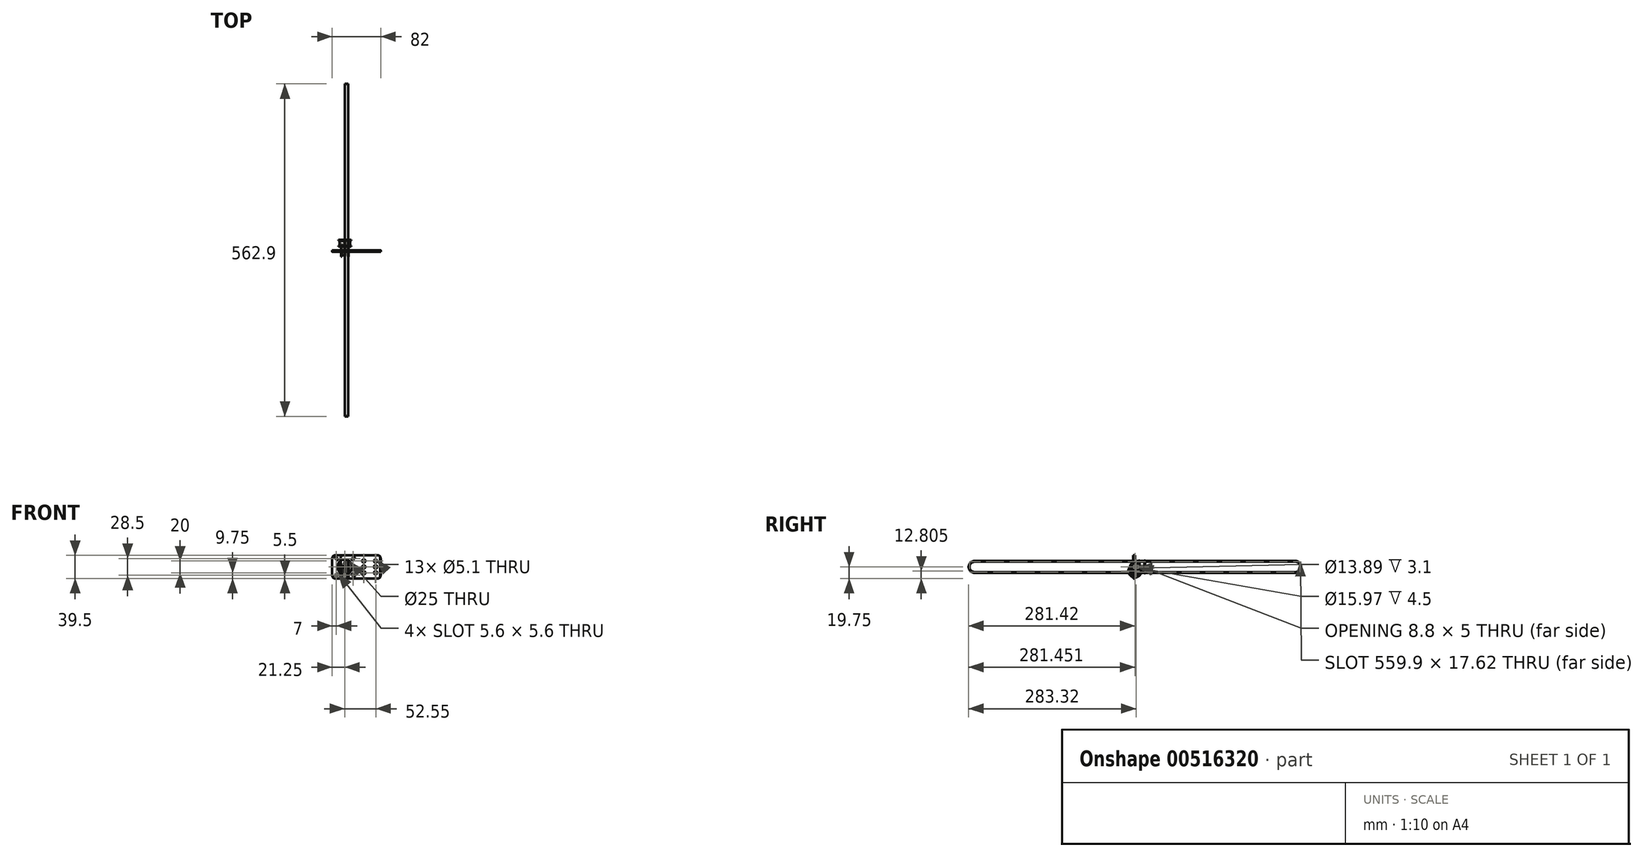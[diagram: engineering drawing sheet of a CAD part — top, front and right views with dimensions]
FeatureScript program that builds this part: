
annotation { "Feature Type Name" : "Feature", "Feature Type Description" : "" }
export const myFeature = defineFeature(function(context is Context, id is Id, definition is map)
    precondition{}
    {
        {
            var Q0;
            Q0=qCreatedBy(makeId("Front.planeOp"),FACE);
            var sketch = newSketch(context, id + "F0", { "sketchPlane" : qUnion([Q0])});
            skCircle(sketch, "E0", {"center": v(0, 0) * mm, "radius": 12.5 * mm});
            skLineSegment(sketch, "E1.bottom", {"start": v(-16.25, 19.75) * mm, "end": v(55.75, 19.75) * mm});
            skLineSegment(sketch, "E1.top", {"start": v(-16.25, -19.75) * mm, "end": v(55.75, -19.75) * mm});
            skLineSegment(sketch, "E1.left", {"start": v(-21.25, 14.75) * mm, "end": v(-21.25, -14.75) * mm});
            skLineSegment(sketch, "E1.right", {"start": v(60.75, 14.75) * mm, "end": v(60.75, -14.75) * mm});
            skLineSegment(sketch, "E2", {"start": v(-15.5, 15.5) * mm, "end": v(-13, 13) * mm, "construction": true});
            skArc(sketch, "E3.0.startCap", {"start": v(-16.6, 14.4) * mm, "mid": v(-16.6, 16.6) * mm, "end": v(-14.4, 16.6) * mm});
            skArc(sketch, "E3.0.endCap", {"start": v(-11.9, 14.1) * mm, "mid": v(-11.9, 11.9) * mm, "end": v(-14.1, 11.9) * mm});
            skLineSegment(sketch, "E3.0.left", {"start": v(-14.4, 16.6) * mm, "end": v(-11.9, 14.1) * mm});
            skLineSegment(sketch, "E3.0.right", {"start": v(-16.6, 14.4) * mm, "end": v(-14.1, 11.9) * mm});
            skLineSegment(sketch, "E4.1.0", {"start": v(-16.6, -14.4) * mm, "end": v(-14.1, -11.9) * mm});
            skArc(sketch, "E4.1.1", {"start": v(-14.1, -11.9) * mm, "mid": v(-11.9, -11.9) * mm, "end": v(-11.9, -14.1) * mm});
            skLineSegment(sketch, "E4.1.2", {"start": v(-15.5, -15.5) * mm, "end": v(-13, -13) * mm});
            skLineSegment(sketch, "E4.1.3", {"start": v(-14.4, -16.6) * mm, "end": v(-11.9, -14.1) * mm});
            skArc(sketch, "E4.1.4", {"start": v(-14.4, -16.6) * mm, "mid": v(-16.6, -16.6) * mm, "end": v(-16.6, -14.4) * mm});
            skLineSegment(sketch, "E4.2.0", {"start": v(14.4, -16.6) * mm, "end": v(11.9, -14.1) * mm});
            skArc(sketch, "E4.2.1", {"start": v(11.9, -14.1) * mm, "mid": v(11.9, -11.9) * mm, "end": v(14.1, -11.9) * mm});
            skLineSegment(sketch, "E4.2.2", {"start": v(15.5, -15.5) * mm, "end": v(13, -13) * mm});
            skLineSegment(sketch, "E4.2.3", {"start": v(16.6, -14.4) * mm, "end": v(14.1, -11.9) * mm});
            skArc(sketch, "E4.2.4", {"start": v(16.6, -14.4) * mm, "mid": v(16.6, -16.6) * mm, "end": v(14.4, -16.6) * mm});
            skLineSegment(sketch, "E4.3.0", {"start": v(16.6, 14.4) * mm, "end": v(14.1, 11.9) * mm});
            skArc(sketch, "E4.3.1", {"start": v(14.1, 11.9) * mm, "mid": v(11.9, 11.9) * mm, "end": v(11.9, 14.1) * mm});
            skLineSegment(sketch, "E4.3.2", {"start": v(15.5, 15.5) * mm, "end": v(13, 13) * mm, "construction": true});
            skLineSegment(sketch, "E4.3.3", {"start": v(14.4, 16.6) * mm, "end": v(11.9, 14.1) * mm});
            skArc(sketch, "E4.3.4", {"start": v(14.4, 16.6) * mm, "mid": v(16.6, 16.6) * mm, "end": v(16.6, 14.4) * mm});
            skCircle(sketch, "E5", {"center": v(32.55, -10) * mm, "radius": 2.55 * mm});
            skCircle(sketch, "E6.0.1.0", {"center": v(32.55, 0) * mm, "radius": 2.55 * mm});
            skCircle(sketch, "E6.0.2.0", {"center": v(32.55, 10) * mm, "radius": 2.55 * mm});
            skCircle(sketch, "E6.1.0.0", {"center": v(52.55, -10) * mm, "radius": 2.55 * mm});
            skCircle(sketch, "E6.1.1.0", {"center": v(52.55, 0) * mm, "radius": 2.55 * mm});
            skCircle(sketch, "E6.1.2.0", {"center": v(52.55, 10) * mm, "radius": 2.55 * mm});
            skLineSegment(sketch, "E6.direction1", {"start": v(32.55, -10) * mm, "end": v(52.55, -10) * mm, "construction": true});
            skLineSegment(sketch, "E6.direction2", {"start": v(32.55, -10) * mm, "end": v(32.55, 0) * mm, "construction": true});
            skPoint(sketch, "E7.visualSharp", {"position": v(-21.25, 19.75) * mm});
            skArc(sketch, "E7.filletArc", {"start": v(-16.25, 19.75) * mm, "mid": v(-19.79, 18.29) * mm, "end": v(-21.25, 14.75) * mm});
            skPoint(sketch, "E8.visualSharp", {"position": v(-21.25, -19.75) * mm});
            skArc(sketch, "E8.filletArc", {"start": v(-21.25, -14.75) * mm, "mid": v(-19.79, -18.29) * mm, "end": v(-16.25, -19.75) * mm});
            skPoint(sketch, "E9.visualSharp", {"position": v(60.75, -19.75) * mm});
            skArc(sketch, "E9.filletArc", {"start": v(55.75, -19.75) * mm, "mid": v(59.29, -18.29) * mm, "end": v(60.75, -14.75) * mm});
            skPoint(sketch, "E10.visualSharp", {"position": v(60.75, 19.75) * mm});
            skArc(sketch, "E10.filletArc", {"start": v(60.75, 14.75) * mm, "mid": v(59.29, 18.29) * mm, "end": v(55.75, 19.75) * mm});
            skSolve(sketch);
        }
        {
            var Q0;
            Q0=makeQuery(id+"F0.imprint","IMPRINT",FACE,{"disambiguationData":[TD([[makeQuery(id+"F0.imprint","IMPRINT",EDGE,{"derivedFrom":sQuery(id+"F0.wireOp",EDGE,"E0")}),-1.0]])]});
            extrude(context, id + "F1", {"entities" : qUnion([Q0]), "depth" : 3 * mm});
        }
        {
            var Q0;
            Q0=qCreatedBy(makeId("Front.planeOp"),FACE);
            var sketch = newSketch(context, id + "F2", { "sketchPlane" : qUnion([Q0])});
            skCircle(sketch, "E11", {"center": v(0, 0) * mm, "radius": 2.55 * mm});
            skLineSegment(sketch, "E12.bottom", {"start": v(-2, 19.75) * mm, "end": v(55, 19.75) * mm});
            skLineSegment(sketch, "E12.top", {"start": v(-2, -19.75) * mm, "end": v(55, -19.75) * mm});
            skLineSegment(sketch, "E12.left", {"start": v(-7, 14.75) * mm, "end": v(-7, -14.75) * mm});
            skLineSegment(sketch, "E12.right", {"start": v(60, 14.75) * mm, "end": v(60, -14.75) * mm});
            skCircle(sketch, "E13", {"center": v(31.79, -10) * mm, "radius": 2.55 * mm});
            skCircle(sketch, "E14.0.1.0", {"center": v(31.79, 0) * mm, "radius": 2.55 * mm});
            skCircle(sketch, "E14.0.2.0", {"center": v(31.79, 10) * mm, "radius": 2.55 * mm});
            skCircle(sketch, "E14.1.0.0", {"center": v(51.8, -10) * mm, "radius": 2.55 * mm});
            skCircle(sketch, "E14.1.1.0", {"center": v(51.8, 0) * mm, "radius": 2.55 * mm});
            skCircle(sketch, "E14.1.2.0", {"center": v(51.8, 10) * mm, "radius": 2.55 * mm});
            skLineSegment(sketch, "E14.direction1", {"start": v(31.79, -10) * mm, "end": v(51.8, -10) * mm, "construction": true});
            skLineSegment(sketch, "E14.direction2", {"start": v(31.79, -10) * mm, "end": v(31.79, 0) * mm, "construction": true});
            skPoint(sketch, "E15.visualSharp", {"position": v(-7, 19.75) * mm});
            skArc(sketch, "E15.filletArc", {"start": v(-2, 19.75) * mm, "mid": v(-5.54, 18.29) * mm, "end": v(-7, 14.75) * mm});
            skPoint(sketch, "E16.visualSharp", {"position": v(60, 19.75) * mm});
            skArc(sketch, "E16.filletArc", {"start": v(60, 14.75) * mm, "mid": v(58.54, 18.29) * mm, "end": v(55, 19.75) * mm});
            skPoint(sketch, "E17.visualSharp", {"position": v(60, -19.75) * mm});
            skArc(sketch, "E17.filletArc", {"start": v(55, -19.75) * mm, "mid": v(58.54, -18.29) * mm, "end": v(60, -14.75) * mm});
            skPoint(sketch, "E18.visualSharp", {"position": v(-7, -19.75) * mm});
            skArc(sketch, "E18.filletArc", {"start": v(-7, -14.75) * mm, "mid": v(-5.54, -18.29) * mm, "end": v(-2, -19.75) * mm});
            skSolve(sketch);
        }
        {
            var Q0;
            Q0=makeQuery(id+"F2.imprint","IMPRINT",FACE,{"disambiguationData":[TD([[makeQuery(id+"F2.imprint","IMPRINT",EDGE,{"derivedFrom":sQuery(id+"F2.wireOp",EDGE,"E11")}),-1.0]])]});
            extrude(context, id + "F3", {"entities" : qUnion([Q0]), "depth" : 3 * mm});
        }
        {
            var Q0;
            Q0=qCreatedBy(makeId("Front.planeOp"),FACE);
            var sketch = newSketch(context, id + "F4", { "sketchPlane" : qUnion([Q0])});
            skLineSegment(sketch, "E19", {"start": v(-6.35, 1.04) * mm, "end": v(-6.35, 4.05) * mm});
            skLineSegment(sketch, "E20", {"start": v(-6.35, 4.05) * mm, "end": v(-4.75, 4.05) * mm});
            skLineSegment(sketch, "E21", {"start": v(-4.75, 4.06) * mm, "end": v(-4.75, 1.8) * mm});
            skLineSegment(sketch, "E22", {"start": v(-4.75, 1.8) * mm, "end": v(4.75, 1.8) * mm});
            skLineSegment(sketch, "E23", {"start": v(4.75, 1.8) * mm, "end": v(4.75, 4.06) * mm});
            skLineSegment(sketch, "E24", {"start": v(4.75, 4.06) * mm, "end": v(6.35, 4.06) * mm});
            skLineSegment(sketch, "E25", {"start": v(6.35, 4.05) * mm, "end": v(6.35, 1.04) * mm});
            skLineSegment(sketch, "E26", {"start": v(6.35, 1.04) * mm, "end": v(1.55, 1.04) * mm});
            skLineSegment(sketch, "E27", {"start": v(1.55, 1.04) * mm, "end": v(1.55, 0) * mm});
            skLineSegment(sketch, "E28", {"start": v(1.55, 0) * mm, "end": v(-1.55, 0) * mm});
            skLineSegment(sketch, "E29", {"start": v(-1.55, 0) * mm, "end": v(-1.55, 1.04) * mm});
            skLineSegment(sketch, "E30", {"start": v(-1.55, 1.04) * mm, "end": v(-6.35, 1.04) * mm});
            skLineSegment(sketch, "E31", {"start": v(0, 0) * mm, "end": v(0, 1.8) * mm, "construction": true});
            skLineSegment(sketch, "E32", {"start": v(-1.55, -6.95) * mm, "end": v(1.55, -6.95) * mm, "construction": true});
            skSolve(sketch);
        }
        {
            var Q0;
            Q0=makeQuery(id+"F4.imprint","IMPRINT",FACE,{"disambiguationData":[TD([[makeQuery(id+"F4.imprint","IMPRINT",EDGE,{"derivedFrom":sQuery(id+"F4.wireOp",EDGE,"E19")}),-1.0]])]});
            var Q1;
            Q1=sQuery(id+"F4.wireOp",EDGE,"E32");
            revolve(context, id + "F5", {"entities" : qUnion([Q0]), "axis" : qUnion([Q1]), "revolveType" : RevolveType.FULL});
        }
        {
            var Q0;
            Q0=makeQuery(id+"F5.opRevolve","SWEPT_EDGE",EDGE,{"disambiguationData":[OSD([sQuery(id+"F4.wireOp",EDGE,"E19"),sQuery(id+"F4.wireOp",EDGE,"E30")])]});
            var Q1;
            Q1=makeQuery(id+"F5.opRevolve","SWEPT_EDGE",EDGE,{"disambiguationData":[OSD([sQuery(id+"F4.wireOp",EDGE,"E25"),sQuery(id+"F4.wireOp",EDGE,"E26")])]});
            chamfer(context, id + "F6", {"entities" : qUnion([Q0, Q1]), "width" : .3 * mm, "tangentPropagation" : true});
        }
        {
            var Q0;
            Q0=qCreatedBy(makeId("Right.planeOp"),FACE);
            var sketch = newSketch(context, id + "F7", { "sketchPlane" : qUnion([Q0])});
            skCircle(sketch, "E33", {"center": v(0, 0) * mm, "radius": 8 * mm});
            skCircle(sketch, "E34", {"center": v(0, 0) * mm, "radius": 2.5 * mm});
            skCircle(sketch, "E35", {"center": v(0, 0) * mm, "radius": 5 * mm});
            skSolve(sketch);
        }
        {
            var Q0;
            Q0=qSketchRegion(id+"F7",true);
            var Q1;
            Q1=makeQuery(id+"F7.imprint","IMPRINT",FACE,{"disambiguationData":[TD([[makeQuery(id+"F7.imprint","IMPRINT",EDGE,{"derivedFrom":sQuery(id+"F7.wireOp",EDGE,"E34")}),-1.0]])]});
            extrude(context, id + "F8", {"entities" : qUnion([Q0, Q1]), "depth" : 5 * mm});
        }
        {
            var Q0;
            Q0=makeQuery(id+"F8.opExtrude","CAP_EDGE",EDGE,{"disambiguationData":[OSD([sQuery(id+"F7.wireOp",EDGE,"E33")])],"isStart":false});
            var Q1;
            Q1=makeQuery(id+"F8.opExtrude","CAP_EDGE",EDGE,{"disambiguationData":[OSD([sQuery(id+"F7.wireOp",EDGE,"E33")])],"isStart":true});
            chamfer(context, id + "F9", {"entities" : qUnion([Q0, Q1]), "width" : .3 * mm, "tangentPropagation" : true});
        }
        {
            var Q0;
            Q0=makeQuery(id+"F7.imprint","IMPRINT",FACE,{"disambiguationData":[TD([[makeQuery(id+"F7.imprint","IMPRINT",EDGE,{"derivedFrom":sQuery(id+"F7.wireOp",EDGE,"E34")}),-1.0]])]});
            extrude(context, id + "F10", {"entities" : qUnion([Q0]), "depth" : 1 * mm});
        }
        {
            var Q0;
            Q0=qCreatedBy(makeId("Right.planeOp"),FACE);
            var sketch = newSketch(context, id + "F11", { "sketchPlane" : qUnion([Q0])});
            skArc(sketch, "E36", {"start": v(-271.17, 8.75) * mm, "mid": v(-279.92, 0) * mm, "end": v(-271.17, -8.75) * mm});
            skArc(sketch, "E37", {"start": v(271.17, -8.81) * mm, "mid": v(279.98, 0) * mm, "end": v(271.17, 8.81) * mm});
            skLineSegment(sketch, "E38", {"start": v(-271.17, 0) * mm, "end": v(271.17, 0) * mm, "construction": true});
            skLineSegment(sketch, "E39", {"start": v(-271.17, 8.75) * mm, "end": v(271.17, 8.81) * mm});
            skLineSegment(sketch, "E40.MirrorCS", {"start": v(-271.17, -8.75) * mm, "end": v(271.17, -8.81) * mm});
            skLineSegment(sketch, "E41.0", {"start": v(-271.17, 10.25) * mm, "end": v(271.17, 10.31) * mm});
            skArc(sketch, "E41.1", {"start": v(-271.17, 10.25) * mm, "mid": v(-281.42, 0) * mm, "end": v(-271.17, -10.25) * mm});
            skLineSegment(sketch, "E41.2", {"start": v(-271.17, -10.25) * mm, "end": v(271.17, -10.31) * mm});
            skArc(sketch, "E41.3", {"start": v(271.17, -10.31) * mm, "mid": v(281.48, 0) * mm, "end": v(271.17, 10.31) * mm});
            skSolve(sketch);
        }
        {
            var Q0;
            Q0=makeQuery(id+"F11.imprint","IMPRINT",FACE,{"disambiguationData":[TD([[makeQuery(id+"F11.imprint","IMPRINT",EDGE,{"derivedFrom":sQuery(id+"F11.wireOp",EDGE,"E36")}),-1.0]])]});
            extrude(context, id + "F12", {"entities" : qUnion([Q0]), "depth" : 6 * mm});
        }
        {
            var Q0;
            Q0=qCreatedBy(makeId("Right.planeOp"),FACE);
            var sketch = newSketch(context, id + "F13", { "sketchPlane" : qUnion([Q0])});
            skLineSegment(sketch, "E42.bottom", {"start": v(0, 6.5) * mm, "end": v(6.3, 6.5) * mm});
            skLineSegment(sketch, "E42.top", {"start": v(0, -6.5) * mm, "end": v(6.3, -6.5) * mm});
            skLineSegment(sketch, "E42.left", {"start": v(0, 6.5) * mm, "end": v(0, -6.5) * mm});
            skLineSegment(sketch, "E42.right", {"start": v(6.3, 6.5) * mm, "end": v(6.3, -6.5) * mm});
            skLineSegment(sketch, "E43.bottom", {"start": v(6.3, 11) * mm, "end": v(7.66, 11) * mm});
            skLineSegment(sketch, "E43.top", {"start": v(6.3, -11) * mm, "end": v(7.66, -11) * mm});
            skLineSegment(sketch, "E43.left", {"start": v(6.3, 11) * mm, "end": v(6.3, -11) * mm});
            skLineSegment(sketch, "E43.right", {"start": v(17.5, 11) * mm, "end": v(17.5, -11) * mm});
            skLineSegment(sketch, "E44", {"start": v(0, 0) * mm, "end": v(17.5, 0) * mm});
            skPoint(sketch, "E45", {"position": v(6.3, 0) * mm});
            skLineSegment(sketch, "E46", {"start": v(7.66, 11) * mm, "end": v(7.66, -11) * mm});
            skLineSegment(sketch, "E47", {"start": v(11.9, 11) * mm, "end": v(11.9, -11) * mm, "construction": true});
            skLineSegment(sketch, "E48.MirrorCS", {"start": v(16.14, 11) * mm, "end": v(16.14, -11) * mm});
            skLineSegment(sketch, "E49", {"start": v(7.9, 8.81) * mm, "end": v(7.9, -8.81) * mm});
            skLineSegment(sketch, "E50.MirrorCS", {"start": v(15.9, 8.81) * mm, "end": v(15.9, -8.81) * mm});
            skLineSegment(sketch, "E51", {"start": v(7.9, 8.81) * mm, "end": v(15.9, 8.81) * mm});
            skLineSegment(sketch, "E52.MirrorCS", {"start": v(7.9, -8.81) * mm, "end": v(15.9, -8.81) * mm});
            skLineSegment(sketch, "E53.trimOffspring", {"start": v(16.14, 11) * mm, "end": v(17.5, 11) * mm});
            skLineSegment(sketch, "E54.trimOffspring", {"start": v(16.14, -11) * mm, "end": v(17.5, -11) * mm});
            skLineSegment(sketch, "E55", {"start": v(7.66, 11) * mm, "end": v(7.9, 8.81) * mm});
            skLineSegment(sketch, "E56.MirrorCS", {"start": v(16.14, 11) * mm, "end": v(15.9, 8.81) * mm});
            skLineSegment(sketch, "E57.MirrorCS", {"start": v(7.66, -11) * mm, "end": v(7.9, -8.81) * mm});
            skLineSegment(sketch, "E58.MirrorCS", {"start": v(16.14, -11) * mm, "end": v(15.9, -8.81) * mm});
            skPoint(sketch, "E59.orphan", {"position": v(7.9, 11) * mm});
            skPoint(sketch, "E60.orphan", {"position": v(15.9, 11) * mm});
            skPoint(sketch, "E61.orphan", {"position": v(15.9, -11) * mm});
            skPoint(sketch, "E62.orphan", {"position": v(7.9, -11) * mm});
            skCircle(sketch, "E63", {"center": v(3.15, 0) * mm, "radius": 1.5 * mm});
            skPoint(sketch, "E64", {"position": v(3.15, 6.5) * mm});
            skLineSegment(sketch, "E65", {"start": v(0, 2.5) * mm, "end": v(17.5, 2.5) * mm});
            skLineSegment(sketch, "E66.MirrorCS", {"start": v(0, -2.5) * mm, "end": v(17.5, -2.5) * mm});
            skSolve(sketch);
        }
        {
            var Q0;
            {var subQ0=sQuery(id+"F13.wireOp",EDGE,"E42.bottom");Q0=makeQuery(id+"F13.imprint","IMPRINT",FACE,{"disambiguationData":[TD([[makeQuery(id+"F13.imprint","IMPRINT",EDGE,{"derivedFrom":subQ0}),-1.0]])]});}
            var Q1;
            {var subQ6=sQuery(id+"F13.wireOp",EDGE,"E43.bottom");Q1=makeQuery(id+"F13.imprint","IMPRINT",FACE,{"disambiguationData":[TD([[makeQuery(id+"F13.imprint","IMPRINT",EDGE,{"derivedFrom":subQ6}),-1.0]])]});}
            var Q2;
            {var subQ0=sQuery(id+"F13.wireOp",EDGE,"E55");Q2=makeQuery(id+"F13.imprint","IMPRINT",FACE,{"disambiguationData":[TD([[makeQuery(id+"F13.imprint","IMPRINT",EDGE,{"derivedFrom":subQ0}),-1.0]])]});}
            var Q3;
            {var subQ0=sQuery(id+"F13.wireOp",EDGE,"E51");Q3=makeQuery(id+"F13.imprint","IMPRINT",FACE,{"disambiguationData":[TD([[makeQuery(id+"F13.imprint","IMPRINT",EDGE,{"derivedFrom":subQ0}),-1.0]])]});}
            var Q4;
            {var subQ0=sQuery(id+"F13.wireOp",EDGE,"E56.MirrorCS");Q4=makeQuery(id+"F13.imprint","IMPRINT",FACE,{"disambiguationData":[TD([[makeQuery(id+"F13.imprint","IMPRINT",EDGE,{"derivedFrom":subQ0}),1.0]])]});}
            var Q5;
            {var subQ0=sQuery(id+"F13.wireOp",EDGE,"E53.trimOffspring");Q5=makeQuery(id+"F13.imprint","IMPRINT",FACE,{"disambiguationData":[TD([[makeQuery(id+"F13.imprint","IMPRINT",EDGE,{"derivedFrom":subQ0}),-1.0]])]});}
            var Q6;
            Q6=sQuery(id+"F13.wireOp",EDGE,"E44");
            revolve(context, id + "F14", {"entities" : qUnion([Q0, Q1, Q2, Q3, Q4, Q5]), "axis" : qUnion([Q6]), "revolveType" : RevolveType.FULL});
        }
        {
            var Q0;
            {var subQ0=sQuery(id+"F13.wireOp",EDGE,"E63");var subQ1=sQuery(id+"F13.wireOp",EDGE,"E44");var subQ2=makeQuery(id+"F13.imprint","INTERSECT",VERTEX,{"disambiguationData":[OD(0.0)],"derivedFrom":[subQ1,subQ0]});Q0=makeQuery(id+"F13.imprint","IMPRINT",FACE,{"disambiguationData":[TD([[makeQuery(id+"F13.imprint","IMPRINT",EDGE,{"disambiguationData":[TD([[subQ2,-1.0]])],"derivedFrom":subQ1}),-1.0]])]});}
            var Q1;
            {var subQ0=sQuery(id+"F13.wireOp",EDGE,"E63");var subQ1=sQuery(id+"F13.wireOp",EDGE,"E44");var subQ2=makeQuery(id+"F13.imprint","INTERSECT",VERTEX,{"disambiguationData":[OD(0.0)],"derivedFrom":[subQ1,subQ0]});Q1=makeQuery(id+"F13.imprint","IMPRINT",FACE,{"disambiguationData":[TD([[makeQuery(id+"F13.imprint","IMPRINT",EDGE,{"disambiguationData":[TD([[subQ2,-1.0]])],"derivedFrom":subQ1}),1.0]])]});}
            extrude(context, id + "F15", {"entities" : qUnion([Q0, Q1]), "operationType" : NewBodyOperationType.REMOVE, "endBound" : BoundingType.THROUGH_ALL, "depth" : 25 * mm});
        }
    });
